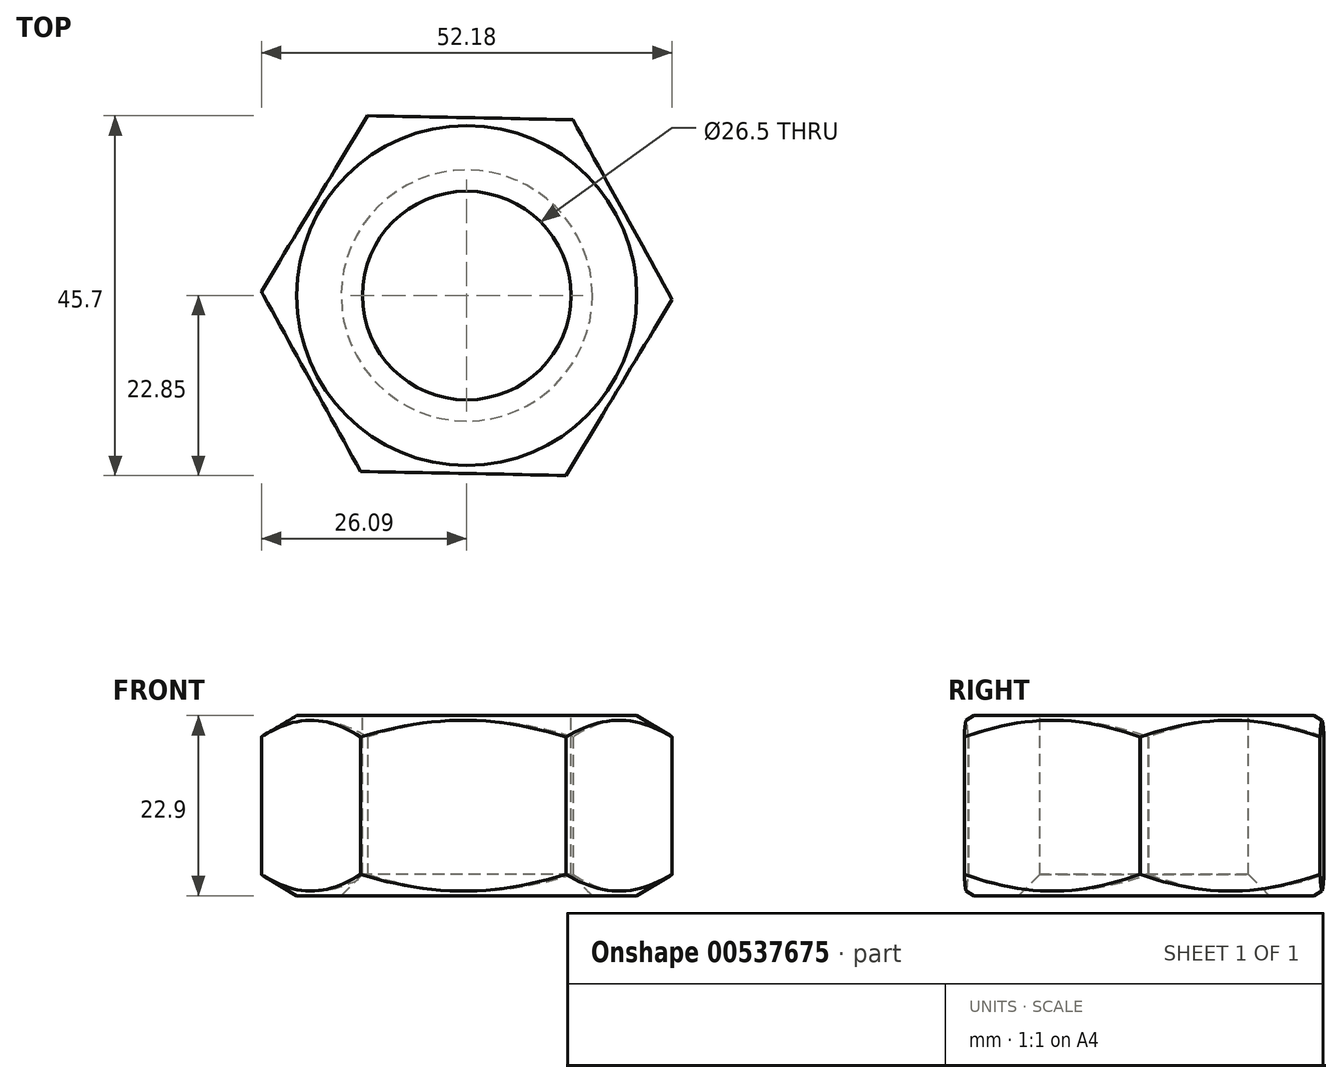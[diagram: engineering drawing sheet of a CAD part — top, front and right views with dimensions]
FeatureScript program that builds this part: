
annotation { "Feature Type Name" : "Feature", "Feature Type Description" : "" }
export const myFeature = defineFeature(function(context is Context, id is Id, definition is map)
    precondition{}
    {
        {
            var Q0;
            Q0=qCreatedBy(makeId("Top.planeOp"),FACE);
            var sketch = newSketch(context, id + "F0", { "sketchPlane" : qUnion([Q0])});
            skCircle(sketch, "E0.cCircle", {"center": v(0, 0) * mm, "radius": 22.6 * mm, "construction": true});
            skLineSegment(sketch, "E0.0", {"start": v(26.1, -0.5) * mm, "end": v(12.6, -22.85) * mm});
            skLineSegment(sketch, "E0.1", {"start": v(12.6, -22.85) * mm, "end": v(-13.48, -22.34) * mm});
            skLineSegment(sketch, "E0.2", {"start": v(-13.48, -22.34) * mm, "end": v(-26.1, 0.5) * mm});
            skLineSegment(sketch, "E0.3", {"start": v(-26.1, 0.5) * mm, "end": v(-12.6, 22.85) * mm});
            skLineSegment(sketch, "E0.4", {"start": v(-12.6, 22.85) * mm, "end": v(13.48, 22.34) * mm});
            skLineSegment(sketch, "E0.5", {"start": v(13.48, 22.34) * mm, "end": v(26.1, -0.5) * mm});
            skPoint(sketch, "E0.0.midPoint", {"position": v(19.35, -11.68) * mm});
            skSolve(sketch);
        }
        {
            var Q0;
            Q0 = qSketchRegion(id + "F0", true);
            extrude(context, id + "F1", {"entities" : qUnion([Q0]), "endBound" : BoundingType.SYMMETRIC, "depth" : 22.9 * mm, "offsetDistance" : 25.4 * mm});
        }
        {
            var Q0;
            Q0=makeQuery(id+"F1.opExtrude","CAP_FACE",FACE,{"disambiguationData":[OSD([sQuery(id+"F0.wireOp",EDGE,"E0.0"),sQuery(id+"F0.wireOp",EDGE,"E0.1"),sQuery(id+"F0.wireOp",EDGE,"E0.2"),sQuery(id+"F0.wireOp",EDGE,"E0.3"),sQuery(id+"F0.wireOp",EDGE,"E0.4"),sQuery(id+"F0.wireOp",EDGE,"E0.5")])],"isStart":false});
            var sketch = newSketch(context, id + "F2", { "sketchPlane" : qUnion([Q0])});
            skCircle(sketch, "E1", {"center": v(0, 0) * mm, "radius": 13.25 * mm});
            skSolve(sketch);
        }
        {
            var Q0;
            Q0 = qSketchRegion(id + "F2", true);
            extrude(context, id + "F3", {"entities" : qUnion([Q0]), "operationType" : NewBodyOperationType.REMOVE, "endBound" : BoundingType.THROUGH_ALL, "oppositeDirection" : true, "depth" : 25.4 * mm, "offsetDistance" : 25.4 * mm});
        }
        {
            var Q0;
            Q0=qCreatedBy(makeId("Front.planeOp"),FACE);
            var sketch = newSketch(context, id + "F4", { "sketchPlane" : qUnion([Q0])});
            skLineSegment(sketch, "E2", {"start": v(21.6, 11.45) * mm, "end": v(26.1, 8.75) * mm});
            skLineSegment(sketch, "E3", {"start": v(26.1, 8.75) * mm, "end": v(26.1, -8.75) * mm});
            skLineSegment(sketch, "E4", {"start": v(26.1, -8.75) * mm, "end": v(21.6, -11.45) * mm});
            skLineSegment(sketch, "E5", {"start": v(21.6, -11.45) * mm, "end": v(34.3, -11.45) * mm});
            skLineSegment(sketch, "E6", {"start": v(34.3, -11.45) * mm, "end": v(34.3, 11.45) * mm});
            skLineSegment(sketch, "E7", {"start": v(34.3, 11.45) * mm, "end": v(21.6, 11.45) * mm});
            skSolve(sketch);
        }
        {
            var Q0;
            Q0 = qSketchRegion(id + "F4", true);
            var Q1;
            Q1=makeQuery(id+"F3.boolean.opBoolean","COPY",FACE,{"derivedFrom":makeQuery(id+"F3.opExtrude","SWEPT_FACE",FACE,{"disambiguationData":[OSD([sQuery(id+"F2.wireOp",EDGE,"E1")])]})});
            revolve(context, id + "F5", {"operationType" : NewBodyOperationType.REMOVE, "entities" : qUnion([Q0]), "axis" : qUnion([Q1]), "revolveType" : RevolveType.FULL, "oppositeDirection" : true});
        }
        {
            var Q0;
            Q0=makeQuery(id+"F3.boolean.opBoolean","COPY",EDGE,{"derivedFrom":makeQuery(id+"F3.opExtrude","CAP_EDGE",EDGE,{"disambiguationData":[OSD([sQuery(id+"F2.wireOp",EDGE,"E1")])],"isStart":true})});
            var Q1;
            Q1=makeQuery(id+"F3.boolean.opBoolean","INTERSECT",EDGE,{"derivedFrom":[makeQuery(id+"F1.opExtrude","CAP_FACE",FACE,{"disambiguationData":[OSD([sQuery(id+"F0.wireOp",EDGE,"E0.0"),sQuery(id+"F0.wireOp",EDGE,"E0.1"),sQuery(id+"F0.wireOp",EDGE,"E0.2"),sQuery(id+"F0.wireOp",EDGE,"E0.3"),sQuery(id+"F0.wireOp",EDGE,"E0.4"),sQuery(id+"F0.wireOp",EDGE,"E0.5")])],"isStart":true}),makeQuery(id+"F3.opExtrude","SWEPT_FACE",FACE,{"disambiguationData":[OSD([sQuery(id+"F2.wireOp",EDGE,"E1")])]})]});
            chamfer(context, id + "F6", {"entities" : qUnion([Q0, Q1]), "width" : 2.7 * mm, "tangentPropagation" : true});
        }
    });
